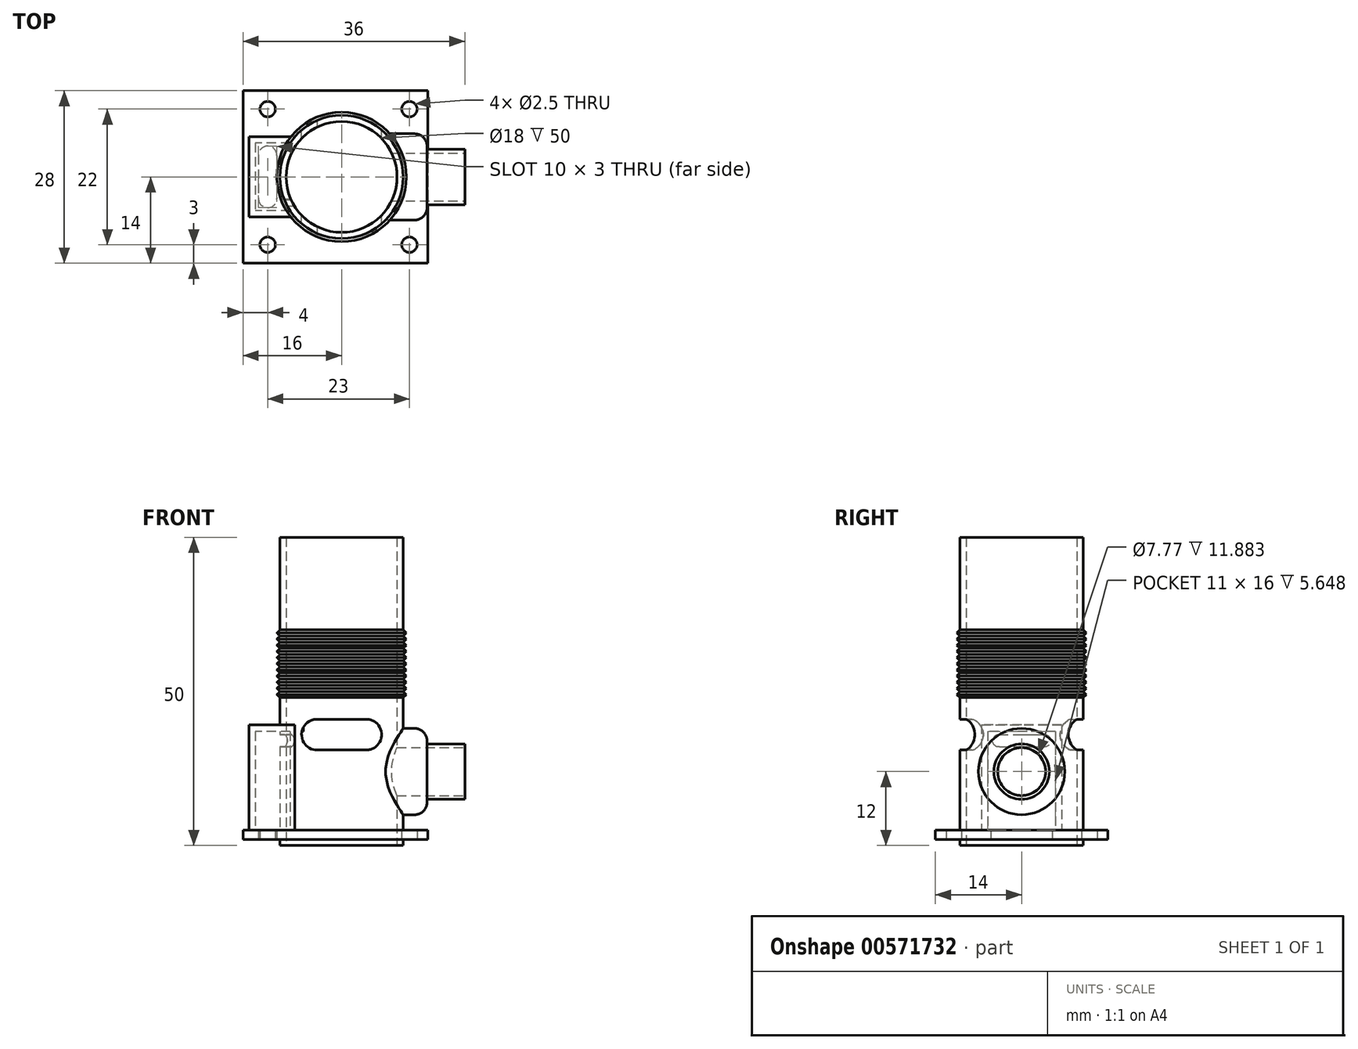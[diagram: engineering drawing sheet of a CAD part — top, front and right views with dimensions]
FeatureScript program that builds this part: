
annotation { "Feature Type Name" : "Feature", "Feature Type Description" : "" }
export const myFeature = defineFeature(function(context is Context, id is Id, definition is map)
    precondition{}
    {
        {
            var Q0;
            Q0=qCreatedBy(makeId("Front.planeOp"),FACE);
            var sketch = newSketch(context, id + "F0", { "sketchPlane" : qUnion([Q0])});
            skLineSegment(sketch, "E0", {"start": v(0, 0) * mm, "end": v(10, 0) * mm});
            skLineSegment(sketch, "E1.0", {"start": v(0, 50) * mm, "end": v(10, 50) * mm});
            skLineSegment(sketch, "E2", {"start": v(0, 0) * mm, "end": v(0, 50) * mm});
            skLineSegment(sketch, "E3.0", {"start": v(10, 0) * mm, "end": v(10, 24) * mm});
            skLineSegment(sketch, "E4", {"start": v(10, 24) * mm, "end": v(10.5, 24.5) * mm});
            skLineSegment(sketch, "E5", {"start": v(10.5, 24.5) * mm, "end": v(10, 25) * mm});
            skLineSegment(sketch, "E6", {"start": v(10, 25) * mm, "end": v(10.5, 25.5) * mm});
            skLineSegment(sketch, "E7", {"start": v(10.5, 25.5) * mm, "end": v(10, 26) * mm});
            skLineSegment(sketch, "E8", {"start": v(10, 26) * mm, "end": v(10.5, 26.5) * mm});
            skLineSegment(sketch, "E9", {"start": v(10.5, 26.5) * mm, "end": v(10, 27) * mm});
            skLineSegment(sketch, "E10", {"start": v(10, 27) * mm, "end": v(10.5, 27.5) * mm});
            skLineSegment(sketch, "E11", {"start": v(10.5, 27.5) * mm, "end": v(10, 28) * mm});
            skLineSegment(sketch, "E12", {"start": v(10, 28) * mm, "end": v(10.5, 28.5) * mm});
            skLineSegment(sketch, "E13", {"start": v(10.5, 28.5) * mm, "end": v(10, 29) * mm});
            skLineSegment(sketch, "E14", {"start": v(10, 29) * mm, "end": v(10.5, 29.5) * mm});
            skLineSegment(sketch, "E15", {"start": v(10.5, 29.5) * mm, "end": v(10, 30) * mm});
            skLineSegment(sketch, "E16", {"start": v(10, 30) * mm, "end": v(10.5, 30.5) * mm});
            skLineSegment(sketch, "E17", {"start": v(10.5, 30.5) * mm, "end": v(10, 31) * mm});
            skLineSegment(sketch, "E18", {"start": v(10, 31) * mm, "end": v(10.5, 31.5) * mm});
            skLineSegment(sketch, "E19", {"start": v(10.5, 31.5) * mm, "end": v(10, 32) * mm});
            skLineSegment(sketch, "E20", {"start": v(10, 32) * mm, "end": v(10.5, 32.5) * mm});
            skLineSegment(sketch, "E21", {"start": v(10.5, 32.5) * mm, "end": v(10, 33) * mm});
            skLineSegment(sketch, "E22", {"start": v(10, 33) * mm, "end": v(10.5, 33.5) * mm});
            skLineSegment(sketch, "E23", {"start": v(10.5, 33.5) * mm, "end": v(10, 34) * mm});
            skLineSegment(sketch, "E24", {"start": v(10, 34) * mm, "end": v(10.5, 34.5) * mm});
            skLineSegment(sketch, "E25", {"start": v(10.5, 34.5) * mm, "end": v(10, 35) * mm});
            skLineSegment(sketch, "E26.trimOffspring", {"start": v(10, 35) * mm, "end": v(10, 50) * mm});
            skSolve(sketch);
        }
        {
            var Q0;
            Q0=makeQuery(id+"F0.imprint","IMPRINT",FACE,{"disambiguationData":[TD([[makeQuery(id+"F0.imprint","IMPRINT",EDGE,{"derivedFrom":sQuery(id+"F0.wireOp",EDGE,"E0")}),1.0]])]});
            var Q1;
            Q1=sQuery(id+"F0.wireOp",EDGE,"E2");
            var Q2;
            Q2=sQuery(id+"F0.wireOp",EDGE,"E26.trimOffspring");
            var Q3;
            Q3=sQuery(id+"F0.wireOp",EDGE,"E3.0");
            var Q4;
            Q4=sQuery(id+"F0.wireOp",EDGE,"E0");
            var Q5;
            Q5=sQuery(id+"F0.wireOp",EDGE,"E1.0");
            var Q6;
            Q6=sQuery(id+"F0.wireOp",EDGE,"E25");
            var Q7;
            Q7=sQuery(id+"F0.wireOp",EDGE,"E4");
            var Q8;
            Q8=sQuery(id+"F0.wireOp",EDGE,"E24");
            var Q9;
            Q9=sQuery(id+"F0.wireOp",EDGE,"E7");
            var Q10;
            Q10=sQuery(id+"F0.wireOp",EDGE,"E22");
            var Q11;
            Q11=sQuery(id+"F0.wireOp",EDGE,"E23");
            var Q12;
            Q12=sQuery(id+"F0.wireOp",EDGE,"E6");
            var Q13;
            Q13=sQuery(id+"F0.wireOp",EDGE,"E5");
            var Q14;
            Q14=sQuery(id+"F0.wireOp",EDGE,"E21");
            var Q15;
            Q15=sQuery(id+"F0.wireOp",EDGE,"E19");
            var Q16;
            Q16=sQuery(id+"F0.wireOp",EDGE,"E18");
            var Q17;
            Q17=sQuery(id+"F0.wireOp",EDGE,"E20");
            var Q18;
            Q18=sQuery(id+"F0.wireOp",EDGE,"E12");
            var Q19;
            Q19=sQuery(id+"F0.wireOp",EDGE,"E9");
            var Q20;
            Q20=sQuery(id+"F0.wireOp",EDGE,"E11");
            var Q21;
            Q21=sQuery(id+"F0.wireOp",EDGE,"E10");
            var Q22;
            Q22=sQuery(id+"F0.wireOp",EDGE,"E15");
            var Q23;
            Q23=sQuery(id+"F0.wireOp",EDGE,"E16");
            var Q24;
            Q24=sQuery(id+"F0.wireOp",EDGE,"E8");
            var Q25;
            Q25=sQuery(id+"F0.wireOp",EDGE,"E14");
            var Q26;
            Q26=sQuery(id+"F0.wireOp",EDGE,"E17");
            var Q27;
            Q27=sQuery(id+"F0.wireOp",EDGE,"E13");
            var Q28;
            Q28=sQuery(id+"F0.wireOp",EDGE,"E2");
            revolve(context, id + "F1", {"entities" : qUnion([Q0]), "surfaceEntities" : qUnion([Q1, Q2, Q3, Q4, Q5, Q6, Q7, Q8, Q9, Q10, Q11, Q12, Q13, Q14, Q15, Q16, Q17, Q18, Q19, Q20, Q21, Q22, Q23, Q24, Q25, Q26, Q27]), "axis" : qUnion([Q28]), "revolveType" : RevolveType.FULL});
        }
        {
            var Q0;
            Q0=qCreatedBy(makeId("Front.planeOp"),FACE);
            var sketch = newSketch(context, id + "F2", { "sketchPlane" : qUnion([Q0])});
            skLineSegment(sketch, "E27", {"start": v(0, 0) * mm, "end": v(74.83, 0) * mm});
            skLineSegment(sketch, "E28", {"start": v(0, 12) * mm, "end": v(0, 19) * mm});
            skLineSegment(sketch, "E29.0", {"start": v(0, 12) * mm, "end": v(20, 12) * mm});
            skLineSegment(sketch, "E30.0", {"start": v(20, 12) * mm, "end": v(20, 16.5) * mm});
            skLineSegment(sketch, "E31.0", {"start": v(0, 19) * mm, "end": v(11.86, 19) * mm});
            skLineSegment(sketch, "E32.0", {"start": v(13.86, 16.5) * mm, "end": v(20, 16.5) * mm});
            skLineSegment(sketch, "E33.trimOffspring", {"start": v(13.86, 16.5) * mm, "end": v(13.86, 17) * mm});
            skPoint(sketch, "E34.visualSharp", {"position": v(13.86, 19) * mm});
            skArc(sketch, "E34.filletArc", {"start": v(13.86, 17) * mm, "mid": v(13.27, 18.41) * mm, "end": v(11.86, 19) * mm});
            skSolve(sketch);
        }
        {
            var Q0;
            Q0=makeQuery(id+"F2.imprint","IMPRINT",FACE,{"disambiguationData":[TD([[makeQuery(id+"F2.imprint","IMPRINT",EDGE,{"derivedFrom":sQuery(id+"F2.wireOp",EDGE,"E28")}),-1.0]])]});
            var Q1;
            Q1=sQuery(id+"F2.wireOp",EDGE,"E29.0");
            revolve(context, id + "F3", {"operationType" : NewBodyOperationType.ADD, "entities" : qUnion([Q0]), "axis" : qUnion([Q1]), "revolveType" : RevolveType.FULL});
        }
        {
            var Q0;
            Q0=qCreatedBy(makeId("Top.planeOp"),FACE);
            cPlane(context, id + "F4", {"entities" : qUnion([Q0]), "cplaneType" : CPlaneType.OFFSET, "offset" : 1 * mm, "width" : 150 * mm, "height" : 150 * mm});
        }
        {
            var Q0;
            Q0=qCreatedBy(id+"F4.planeOp",FACE);
            var sketch = newSketch(context, id + "F5", { "sketchPlane" : qUnion([Q0])});
            skPoint(sketch, "E35.orphan", {"position": v(-16, 19.2) * mm});
            skPoint(sketch, "E36.orphan", {"position": v(-16, -19.2) * mm});
            skPoint(sketch, "E37.orphan", {"position": v(43.76, -14) * mm});
            skPoint(sketch, "E38.orphan", {"position": v(43.76, 14) * mm});
            skLineSegment(sketch, "E39", {"start": v(-16, 14) * mm, "end": v(-16, -14) * mm});
            skLineSegment(sketch, "E40", {"start": v(-16, 14) * mm, "end": v(14, 14) * mm});
            skLineSegment(sketch, "E41", {"start": v(14, 14) * mm, "end": v(14, -14) * mm});
            skLineSegment(sketch, "E42", {"start": v(-16, -14) * mm, "end": v(14, -14) * mm});
            skCircle(sketch, "E43", {"center": v(-12, 11) * mm, "radius": 1.25 * mm});
            skCircle(sketch, "E44", {"center": v(11, 11) * mm, "radius": 1.25 * mm});
            skCircle(sketch, "E45", {"center": v(-12, -11) * mm, "radius": 1.25 * mm});
            skCircle(sketch, "E46", {"center": v(11, -11) * mm, "radius": 1.25 * mm});
            skArc(sketch, "E47", {"start": v(-10.5, 3.5) * mm, "mid": v(-12, 5) * mm, "end": v(-13.5, 3.5) * mm});
            skArc(sketch, "E48.MirrorC", {"start": v(-10.5, -3.5) * mm, "mid": v(-12, -5) * mm, "end": v(-13.5, -3.5) * mm});
            skLineSegment(sketch, "E49", {"start": v(-13.5, 3.5) * mm, "end": v(-13.5, -3.5) * mm});
            skLineSegment(sketch, "E50", {"start": v(-10.5, 3.5) * mm, "end": v(-10.5, -3.5) * mm});
            skSolve(sketch);
        }
        {
            var Q0;
            Q0=makeQuery(id+"F5.imprint","IMPRINT",FACE,{"disambiguationData":[TD([[makeQuery(id+"F5.imprint","IMPRINT",EDGE,{"derivedFrom":sQuery(id+"F5.wireOp",EDGE,"E39")}),1.0]])]});
            extrude(context, id + "F6", {"entities" : qUnion([Q0]), "operationType" : NewBodyOperationType.ADD, "depth" : 1.5 * mm, "offsetDistance" : 25 * mm});
        }
        {
            var Q0;
            Q0=qCreatedBy(makeId("Front.planeOp"),FACE);
            var sketch = newSketch(context, id + "F7", { "sketchPlane" : qUnion([Q0])});
            skArc(sketch, "E51", {"start": v(4, 15.5) * mm, "mid": v(6.5, 18) * mm, "end": v(4, 20.5) * mm});
            skArc(sketch, "E52.MirrorC", {"start": v(-3.94, 15.5) * mm, "mid": v(-6.5, 17.97) * mm, "end": v(-4, 20.5) * mm});
            skLineSegment(sketch, "E53", {"start": v(-4, 20.5) * mm, "end": v(4, 20.5) * mm});
            skLineSegment(sketch, "E54", {"start": v(-3.94, 15.5) * mm, "end": v(4, 15.5) * mm});
            skSolve(sketch);
        }
        {
            var Q0;
            Q0 = qSketchRegion(id + "F7", true);
            extrude(context, id + "F8", {"entities" : qUnion([Q0]), "operationType" : NewBodyOperationType.REMOVE, "depth" : 25 * mm, "offsetDistance" : 25 * mm, "symmetric" : true});
        }
        {
            var Q0;
            Q0=makeQuery(id+"F6.opExtrude","CAP_FACE",FACE,{"disambiguationData":[OSD([sQuery(id+"F5.wireOp",EDGE,"E39"),sQuery(id+"F5.wireOp",EDGE,"E40"),sQuery(id+"F5.wireOp",EDGE,"E41"),sQuery(id+"F5.wireOp",EDGE,"E42"),sQuery(id+"F5.wireOp",EDGE,"E43"),sQuery(id+"F5.wireOp",EDGE,"E44"),sQuery(id+"F5.wireOp",EDGE,"E45"),sQuery(id+"F5.wireOp",EDGE,"E46"),sQuery(id+"F5.wireOp",EDGE,"E47"),sQuery(id+"F5.wireOp",EDGE,"E48.MirrorC"),sQuery(id+"F5.wireOp",EDGE,"E49"),sQuery(id+"F5.wireOp",EDGE,"E50")])],"isStart":false});
            var sketch = newSketch(context, id + "F9", { "sketchPlane" : qUnion([Q0])});
            skLineSegment(sketch, "E55.0", {"start": v(-7.2, 5.5) * mm, "end": v(-14, 5.5) * mm});
            skLineSegment(sketch, "E56.0", {"start": v(-7.2, -5.5) * mm, "end": v(-14, -5.5) * mm});
            skLineSegment(sketch, "E57.0", {"start": v(-14, 0) * mm, "end": v(-14, 5.5) * mm});
            skLineSegment(sketch, "E58.0", {"start": v(-15, 0) * mm, "end": v(-15, 6.5) * mm});
            skLineSegment(sketch, "E59.0", {"start": v(-7.2, -6.5) * mm, "end": v(-15, -6.5) * mm});
            skLineSegment(sketch, "E60.0", {"start": v(-7.2, 6.5) * mm, "end": v(-15, 6.5) * mm});
            skLineSegment(sketch, "E61.0", {"start": v(-14, 0) * mm, "end": v(-14, -5.5) * mm});
            skLineSegment(sketch, "E62.0", {"start": v(-15, 0) * mm, "end": v(-15, -6.5) * mm});
            skLineSegment(sketch, "E63", {"start": v(-7.2, 6.5) * mm, "end": v(-7.2, 5.5) * mm});
            skLineSegment(sketch, "E64.trimOffspring", {"start": v(-7.2, -5.5) * mm, "end": v(-7.2, -6.5) * mm});
            skSolve(sketch);
        }
        {
            var Q0;
            Q0 = qSketchRegion(id + "F9", true);
            extrude(context, id + "F10", {"entities" : qUnion([Q0]), "operationType" : NewBodyOperationType.ADD, "depth" : 16 * mm, "offsetDistance" : 25 * mm});
        }
        {
            var Q0;
            Q0=makeQuery(id+"F10.opExtrude","CAP_FACE",FACE,{"disambiguationData":[OSD([sQuery(id+"F9.wireOp",EDGE,"E55.0"),sQuery(id+"F9.wireOp",EDGE,"E56.0"),sQuery(id+"F9.wireOp",EDGE,"E57.0"),sQuery(id+"F9.wireOp",EDGE,"E58.0"),sQuery(id+"F9.wireOp",EDGE,"E59.0"),sQuery(id+"F9.wireOp",EDGE,"E60.0"),sQuery(id+"F9.wireOp",EDGE,"E61.0"),sQuery(id+"F9.wireOp",EDGE,"E62.0"),sQuery(id+"F9.wireOp",EDGE,"E63"),sQuery(id+"F9.wireOp",EDGE,"E64.trimOffspring")])],"isStart":false});
            var sketch = newSketch(context, id + "F11", { "sketchPlane" : qUnion([Q0])});
            skLineSegment(sketch, "E65", {"start": v(-15, 6.5) * mm, "end": v(-15, -6.5) * mm});
            skLineSegment(sketch, "E66", {"start": v(-15, -6.5) * mm, "end": v(-4.92, -6.5) * mm});
            skLineSegment(sketch, "E67", {"start": v(-4.92, -6.5) * mm, "end": v(-4.92, 6.5) * mm});
            skLineSegment(sketch, "E68", {"start": v(-15, 6.5) * mm, "end": v(-4.92, 6.5) * mm});
            skSolve(sketch);
        }
        {
            var Q0;
            Q0 = qSketchRegion(id + "F11", true);
            extrude(context, id + "F12", {"entities" : qUnion([Q0]), "operationType" : NewBodyOperationType.ADD, "depth" : 1.1 * mm, "offsetDistance" : 25 * mm});
        }
        {
            var Q0;
            Q0=qCreatedBy(makeId("Right.planeOp"),FACE);
            var sketch = newSketch(context, id + "F13", { "sketchPlane" : qUnion([Q0])});
            skArc(sketch, "E69", {"start": v(3.7, 16) * mm, "mid": v(4.7, 17) * mm, "end": v(3.7, 18) * mm});
            skArc(sketch, "E70.MirrorC", {"start": v(-3.6, 16) * mm, "mid": v(-4.7, 16.96) * mm, "end": v(-3.68, 18) * mm});
            skLineSegment(sketch, "E71", {"start": v(-3.68, 18) * mm, "end": v(3.7, 18) * mm});
            skLineSegment(sketch, "E72", {"start": v(-3.8, 16) * mm, "end": v(3.7, 16) * mm});
            skSolve(sketch);
        }
        {
            var Q0;
            Q0 = qSketchRegion(id + "F13", true);
            extrude(context, id + "F14", {"entities" : qUnion([Q0]), "operationType" : NewBodyOperationType.REMOVE, "oppositeDirection" : true, "depth" : 11 * mm, "offsetDistance" : 25 * mm});
        }
        {
            var Q0;
            Q0=qCreatedBy(makeId("Top.planeOp"),FACE);
            var sketch = newSketch(context, id + "F15", { "sketchPlane" : qUnion([Q0])});
            skCircle(sketch, "E73", {"center": v(0, 0) * mm, "radius": 9 * mm});
            skSolve(sketch);
        }
        {
            var Q0;
            Q0 = qSketchRegion(id + "F15", true);
            extrude(context, id + "F16", {"entities" : qUnion([Q0]), "operationType" : NewBodyOperationType.REMOVE, "endBound" : BoundingType.THROUGH_ALL, "depth" : 25 * mm, "offsetDistance" : 25 * mm});
        }
        {
            var Q0;
            Q0=makeQuery(id+"F3.opRevolve","SWEPT_FACE",FACE,{"disambiguationData":[OSD([sQuery(id+"F2.wireOp",EDGE,"E30.0")])]});
            var sketch = newSketch(context, id + "F17", { "sketchPlane" : qUnion([Q0])});
            skCircle(sketch, "E74", {"center": v(0, 12) * mm, "radius": 3.89 * mm});
            skSolve(sketch);
        }
        {
            var Q0;
            Q0=makeQuery(id+"F17.imprint","IMPRINT",FACE,{"disambiguationData":[TD([[makeQuery(id+"F17.imprint","IMPRINT",EDGE,{"derivedFrom":sQuery(id+"F17.wireOp",EDGE,"E74")}),1.0]])]});
            var Q1;
            Q1=sQuery(id+"F17.wireOp",EDGE,"E74");
            extrude(context, id + "F18", {"entities" : qUnion([Q0]), "operationType" : NewBodyOperationType.REMOVE, "surfaceEntities" : qUnion([Q1]), "oppositeDirection" : true, "depth" : 18 * mm, "offsetDistance" : 25 * mm});
        }
    });
